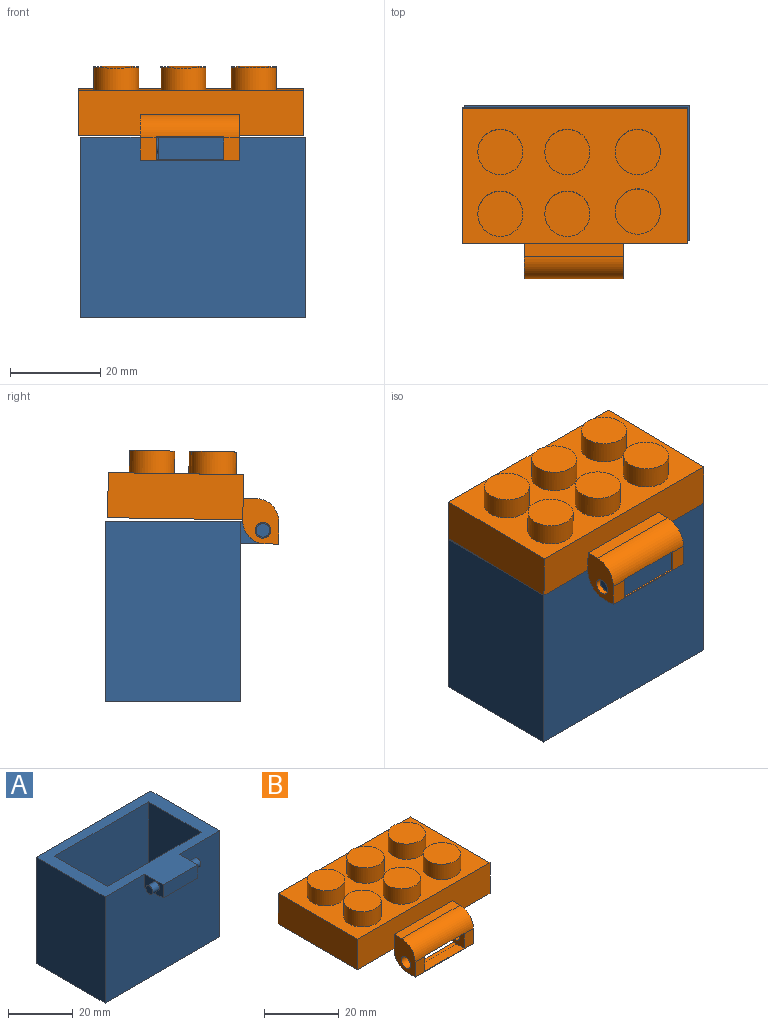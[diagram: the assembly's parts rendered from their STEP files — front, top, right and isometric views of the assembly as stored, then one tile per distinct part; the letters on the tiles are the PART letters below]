
ASSEMBLY  parts=2 mates=1
PART A: 19 faces, bbox 50x38x40 mm
  f0: plane 50x40mm, normal (0,1,0), area 2000mm2, adj f1,f7,f8,f9
  f1: plane 40x30mm, normal (-1,0,0), area 1200mm2, adj f0,f2,f8,f9
  f2: plane 50x40mm, normal (0,-1,0), area 1925mm2, adj f1,f7,f8,f9,f11,f12,f13
  f3: plane 35x22.96mm, normal (1,0,0), area 803.4mm2, adj f4,f6,f8,f10
  f4: plane 40.92x35mm, normal (0,-1,0), area 1432.2mm2, adj f3,f5,f8,f10
  f5: plane 35x22.96mm, normal (-1,0,0), area 803.4mm2, adj f4,f6,f8,f10
  f6: plane 40.92x35mm, normal (0,1,0), area 1432.2mm2, adj f3,f5,f8,f10
  f7: plane 40x30mm, normal (1,0,0), area 1200mm2, adj f0,f2,f8,f9
  f8: plane 50x38mm, normal (0,0,1), area 680.7mm2, adj f0,f1,f2,f3,f4,f5,f6,f7
  f9: plane 50x30mm, normal (0,0,-1), area 1500mm2, adj f0,f1,f2,f7
  f10: plane 40.92x22.96mm, normal (0,0,1), area 939.3mm2, adj f3,f4,f5,f6
  f11: plane 8x5mm, normal (-1,0,0), area 32.9mm2, adj f2,f8,f12,f14,f17
  f12: plane 15x8mm, normal (0,0,-1), area 120mm2, adj f2,f11,f13,f14
  f13: plane 8x5mm, normal (1,0,0), area 32.9mm2, adj f2,f8,f12,f14,f15
  f14: plane 15x5mm, normal (0,-1,0), area 75mm2, adj f8,f11,f12,f13
  f15: cylinder r=1.5mm len=3mm, axis (-1,0,0), area 28.3mm2, adj f13,f16
  f16: plane 3x3mm, normal (1,0,0), area 7.1mm2, adj f15
  f17: cylinder r=1.5mm len=3mm, axis (1,0,0), area 28.3mm2, adj f11,f18
  f18: plane 3x3mm, normal (-1,0,0), area 7.1mm2, adj f17
PART B: 32 faces, bbox 50x38x20.3 mm
  f0: plane 22x0.2mm, normal (0,1,0), area 3.6mm2, adj f3,f4,f10,f26,f28,f29,f30
  f1: plane 22x4.92mm, normal (0,-1,0), area 36.4mm2, adj f3,f4,f24,f27,f28,f29,f31
  f2: cylinder r=1.75mm len=3.5mm, axis (1,0,0), area 38.3mm2, adj f3,f29
  f3: plane 10x8mm, normal (1,0,0), area 59.3mm2, adj f0,f1,f2,f7,f23,f24,f30,f31
  f4: plane 10x8mm, normal (-1,0,0), area 59.3mm2, adj f0,f1,f7,f23,f24,f25,f30,f31
  f5: plane 50x10mm, normal (0,1,0), area 500mm2, adj f6,f8,f9,f10
  f6: plane 30x10mm, normal (-1,0,0), area 300mm2, adj f5,f7,f9,f10
  f7: plane 50x10mm, normal (0,-1,0), area 396.1mm2, adj f3,f4,f6,f8,f9,f10,f23
  f8: plane 30x10mm, normal (1,0,0), area 300mm2, adj f5,f7,f9,f10
  f9: plane 50x30mm, normal (0,0,1), area 1028.8mm2, adj f5,f6,f7,f8,f11,f13,f15,f17
  f10: plane 50x30mm, normal (0,0,-1), area 1500mm2, adj f0,f5,f6,f7,f8
  f11: cylinder r=5mm len=10mm, axis (0,0,-1), area 157.1mm2, adj f9,f12
  f12: plane 10x10mm, normal (0,0,1), area 78.5mm2, adj f11
  f13: cylinder r=5mm len=10mm, axis (0,0,-1), area 157.1mm2, adj f9,f14
  f14: plane 10x10mm, normal (0,0,1), area 78.5mm2, adj f13
  f15: cylinder r=5mm len=10mm, axis (0,0,-1), area 157.1mm2, adj f9,f16
  f16: plane 10x10mm, normal (0,0,1), area 78.5mm2, adj f15
  f17: cylinder r=5mm len=10mm, axis (0,0,-1), area 157.1mm2, adj f9,f18
  f18: plane 10x10mm, normal (0,0,1), area 78.5mm2, adj f17
  f19: cylinder r=5mm len=10mm, axis (0,0,-1), area 157.1mm2, adj f9,f20
  f20: plane 10x10mm, normal (0,0,1), area 78.5mm2, adj f19
  f21: cylinder r=5mm len=10mm, axis (0,0,-1), area 157.1mm2, adj f9,f22
  f22: plane 10x10mm, normal (0,0,1), area 78.5mm2, adj f21
  f23: plane 22x2.92mm, normal (0,0,1), area 64.2mm2, adj f3,f4,f7,f31
  f24: plane 22x2.92mm, normal (0,0,-1), area 64.2mm2, adj f1,f3,f4,f30
  f25: cylinder r=1.75mm len=3.52mm, axis (1,0,0), area 38.7mm2, adj f4,f28
  f26: plane 15x8mm, normal (0,0,-1), area 119.9mm2, adj f0,f28,f29,f31
  f27: plane 15x4.06mm, normal (0,0,1), area 61mm2, adj f1,f28,f29,f30
  f28: plane 8x5mm, normal (1,0,0), area 25.4mm2, adj f0,f1,f25,f26,f27,f30,f31
  f29: plane 8x5mm, normal (-1,0,0), area 25.4mm2, adj f0,f1,f2,f26,f27,f30,f31
  f30: cylinder r=5.08mm len=22mm, axis (1,0,0), area 73.2mm2, adj f0,f3,f4,f24,f27,f28,f29
  f31: cylinder r=5.08mm len=22mm, axis (1,0,0), area 172.4mm2, adj f1,f3,f4,f23,f26,f28,f29
PLACE A t=(-4.1,9.01,15.77)mm fixed
PLACE B rot(axis=(1,0,0),0.9deg) t=(-1.58,20.44,56.56)mm
MATE revolute B.f2 <-> A.f15  axis (1,0,0) through (7.06,-13.46,53.77)mm
